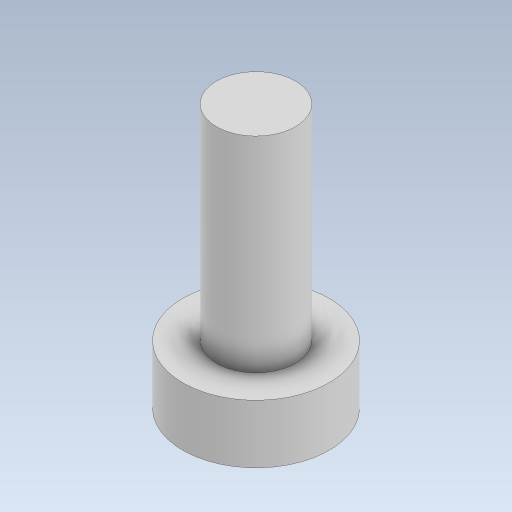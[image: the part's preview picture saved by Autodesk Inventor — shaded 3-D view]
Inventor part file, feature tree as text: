
AUTODESK INVENTOR PART (.ipt)
format: ipt  version: 2023.5 (Build 275446000, 446)  size: 99,840 bytes
history: native  units: mm
features: extrude x2, sketch x1
ambient origin geometry x8: Origin, YZ Plane, XZ Plane, XY Plane, X Axis, Y Axis, Z Axis, Center Point
bodies: Solid1 (feature_tree)
feature tree (3):
  sketch  "Sketch1"  dims[d0=5.0mm d1=2.7mm d2=9.0mm d3=0.0mm d4=2.0mm d5=0.0mm]
  extrude  "Extrusion1"  Depth=2.0mm
  extrude  "Extrusion2"  Depth=9.0mm TaperAngle=0.0deg
